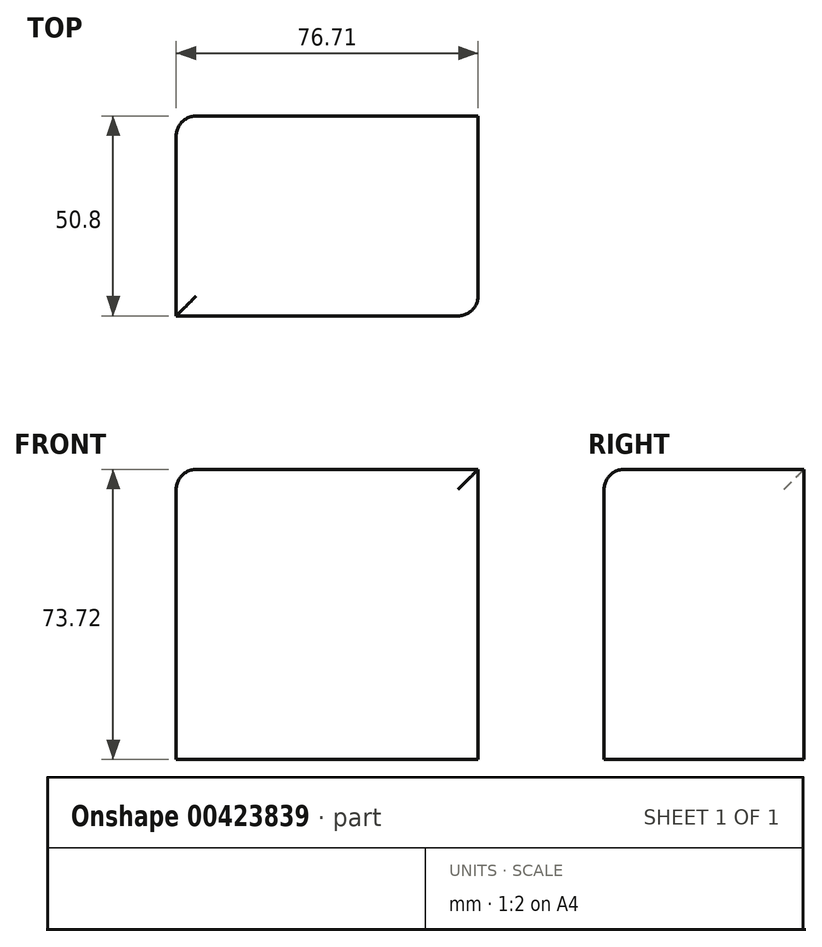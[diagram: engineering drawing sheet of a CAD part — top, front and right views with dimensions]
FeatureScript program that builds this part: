
annotation { "Feature Type Name" : "Feature", "Feature Type Description" : "" }
export const myFeature = defineFeature(function(context is Context, id is Id, definition is map)
    precondition{}
    {
        {
            var Q0;
            Q0=qCreatedBy(makeId("Front.planeOp"),FACE);
            var sketch = newSketch(context, id + "F0", { "sketchPlane" : qUnion([Q0])});
            skLineSegment(sketch, "E0.bottom", {"start": v(-42.87, 49.15) * mm, "end": v(33.84, 49.15) * mm});
            skLineSegment(sketch, "E0.top", {"start": v(-42.87, -24.57) * mm, "end": v(33.84, -24.57) * mm});
            skLineSegment(sketch, "E0.left", {"start": v(-42.87, 49.15) * mm, "end": v(-42.87, -24.57) * mm});
            skLineSegment(sketch, "E0.right", {"start": v(33.84, 49.15) * mm, "end": v(33.84, -24.57) * mm});
            skSolve(sketch);
        }
        {
            var Q0;
            Q0=makeQuery(id+"F0.imprint","IMPRINT",FACE,{"disambiguationData":[TD([[makeQuery(id+"F0.imprint","IMPRINT",EDGE,{"derivedFrom":sQuery(id+"F0.wireOp",EDGE,"E0.bottom")}),-1.0]])]});
            extrude(context, id + "F1", {"entities" : qUnion([Q0]), "endBound" : BoundingType.SYMMETRIC, "depth" : 50.8 * mm});
        }
        {
            var Q0;
            Q0=makeQuery(id+"F1.opExtrude","CAP_EDGE",EDGE,{"disambiguationData":[OSD([sQuery(id+"F0.wireOp",EDGE,"E0.right")])],"isStart":false});
            var Q1;
            Q1=makeQuery(id+"F1.opExtrude","CAP_EDGE",EDGE,{"disambiguationData":[OSD([sQuery(id+"F0.wireOp",EDGE,"E0.bottom")])],"isStart":false});
            var Q2;
            Q2=makeQuery(id+"F1.opExtrude","SWEPT_EDGE",EDGE,{"disambiguationData":[OSD([sQuery(id+"F0.wireOp",EDGE,"E0.bottom"),sQuery(id+"F0.wireOp",EDGE,"E0.left")])]});
            var Q3;
            Q3=makeQuery(id+"F1.opExtrude","CAP_EDGE",EDGE,{"disambiguationData":[OSD([sQuery(id+"F0.wireOp",EDGE,"E0.left")])],"isStart":true});
            fillet(context, id + "F2", {"entities" : qUnion([Q0, Q1, Q2, Q3]), "radius" : 5.08 * mm, "tangentPropagation" : true, "allowEdgeOverflow" : false});
        }
    });
